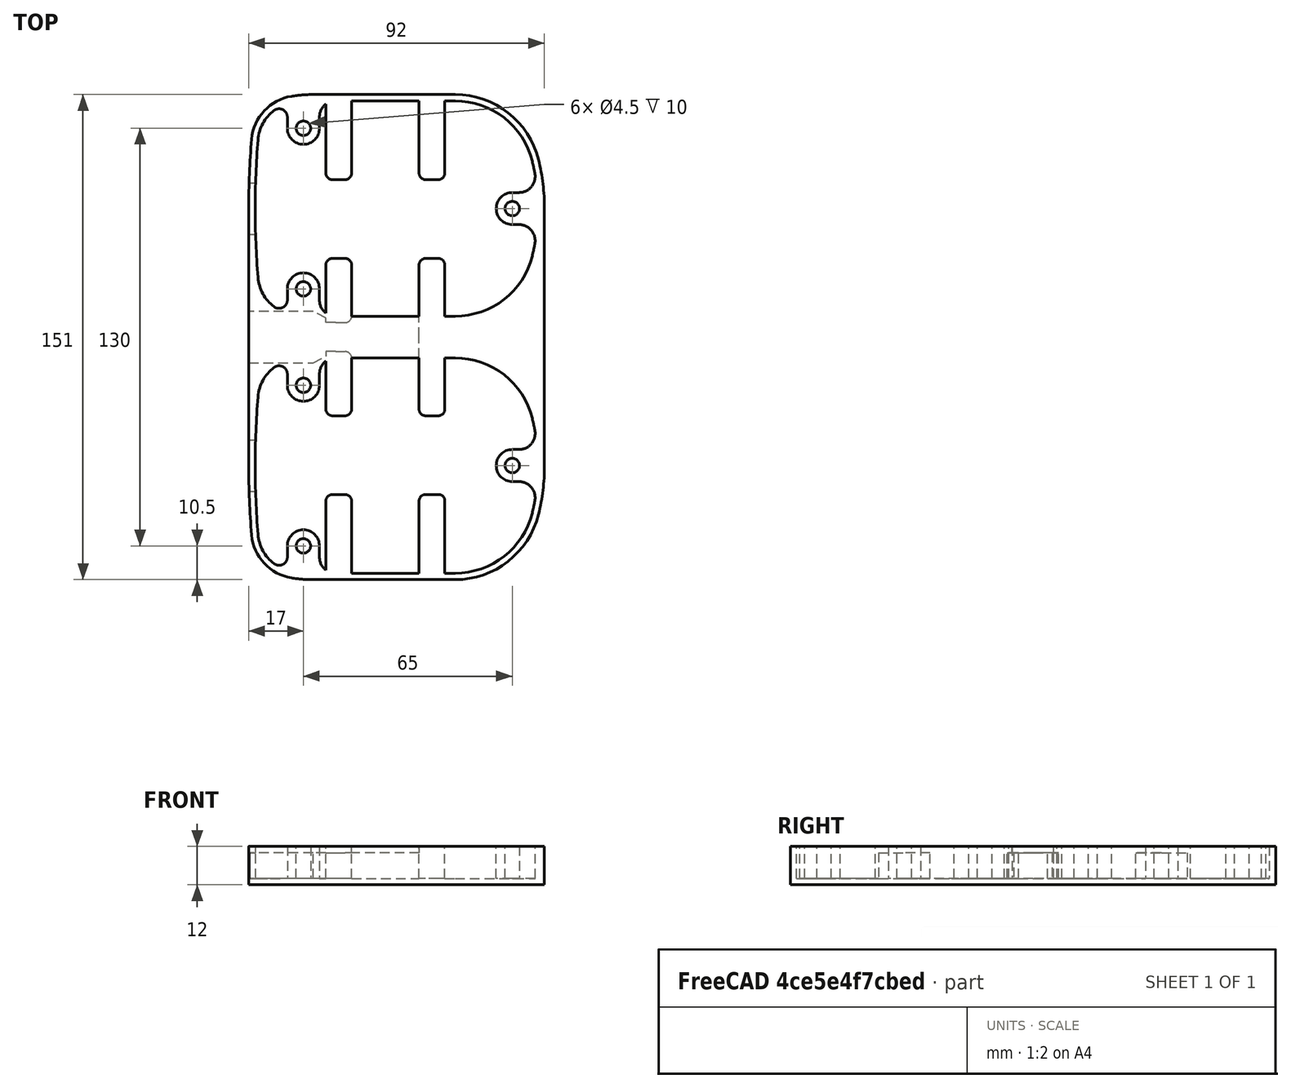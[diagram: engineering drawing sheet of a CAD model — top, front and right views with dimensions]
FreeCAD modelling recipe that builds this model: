
FCSTD DOCUMENT  (FreeCAD 1.0R39285 (Git))
Label: Makita LXT  - 18V - 2 x Bottom
License: Creative Commons Attribution 4.0
LicenseURL: https://creativecommons.org/licenses/by/4.0/
objects: Sketcher::SketchObject×6, PartDesign::Pocket×4, Mesh::Feature×3, PartDesign::Pad×2, Part::Feature×1, PartDesign::Body×1
note: 32 computed .brp shape members not serialized (recipe doc carries the construction recipe); baked Part::Feature solids carry a one-line shape summary decoded from their .brp

FEATURE [Mesh::Feature] XT60_top
  Placement = pos=(-27.47,40,-11) rot=(0,0,1;0rad)
FEATURE [Mesh::Feature] XT60_top001
  Placement = pos=(-27.47,-40,2) rot=(0,0,1;0rad)
FEATURE [Sketcher::SketchObject] Sketch
  ArcFitTolerance = 0
  AttachmentSupport = -> [XY_Plane]
  FullyConstrained = true
  MakeInternals = false
  MapMode = 5
  sketch-geometry (16):
    g0: ArcOfCircle CenterX=259.65 CenterY=40 CenterZ=0 NormalX=0 NormalY=0 NormalZ=1 AngleXU=0 Radius=259.65 StartAngle=3.05831 EndAngle=3.14159
    g1: ArcOfCircle CenterX=15.6319 CenterY=60.3702 CenterZ=0 NormalX=0 NormalY=0 NormalZ=1 AngleXU=0 Radius=14.7831 StartAngle=1.7292 EndAngle=3.05831
    g2: LineSegment StartX=20 StartY=75.5 StartZ=0 EndX=64.2 EndY=75.5 EndZ=0
    g3: ArcOfCircle CenterX=64.2 CenterY=48.7705 CenterZ=0 NormalX=0 NormalY=0 NormalZ=1 AngleXU=0 Radius=26.7295 StartAngle=0.24292 EndAngle=1.5708
    g4: ArcOfCircle CenterX=28.8084 CenterY=40 CenterZ=0 NormalX=0 NormalY=0 NormalZ=1 AngleXU=0 Radius=63.1916 StartAngle=0 EndAngle=0.24292
    g5: ArcOfCircle CenterX=20 CenterY=33.0247 CenterZ=0 NormalX=0 NormalY=0 NormalZ=1 AngleXU=0 Radius=42.4753 StartAngle=1.5708 EndAngle=1.7292
    g6: LineSegment StartX=0 StartY=40 StartZ=0 EndX=0 EndY=0 EndZ=0
    g7: LineSegment StartX=92 StartY=40 StartZ=0 EndX=92 EndY=0 EndZ=0
    g8: ArcOfCircle CenterX=259.65 CenterY=-40 CenterZ=0 NormalX=0 NormalY=0 NormalZ=1 AngleXU=0 Radius=259.65 StartAngle=3.14159 EndAngle=3.22488
    g9: ArcOfCircle CenterX=15.6319 CenterY=-60.3702 CenterZ=0 NormalX=0 NormalY=0 NormalZ=1 AngleXU=0 Radius=14.7831 StartAngle=3.22488 EndAngle=4.55399
    g10: LineSegment StartX=20 StartY=-75.5 StartZ=0 EndX=64.2 EndY=-75.5 EndZ=0
    g11: ArcOfCircle CenterX=64.2 CenterY=-48.7705 CenterZ=0 NormalX=0 NormalY=0 NormalZ=1 AngleXU=0 Radius=26.7295 StartAngle=4.71239 EndAngle=6.04026
    g12: ArcOfCircle CenterX=28.8084 CenterY=-40 CenterZ=0 NormalX=0 NormalY=0 NormalZ=1 AngleXU=0 Radius=63.1916 StartAngle=6.04026 EndAngle=6.28319
    g13: ArcOfCircle CenterX=20 CenterY=-33.0247 CenterZ=0 NormalX=0 NormalY=0 NormalZ=1 AngleXU=0 Radius=42.4753 StartAngle=4.55399 EndAngle=4.71239
    g14: LineSegment StartX=0 StartY=-40 StartZ=0 EndX=0 EndY=0 EndZ=0
    g15: LineSegment StartX=92 StartY=-40 StartZ=0 EndX=92 EndY=0 EndZ=0
  constraints (46):
    c: Horizontal(g2)
    c: DistanceX(g2) = 20
    c: DistanceY(g2) = 75.5
    c: DistanceX(g2,g2) = 44.2
    c: Tangent(g4,g3) = -1.5708
    c: Tangent(g3,g2) = 1.5708
    c: DistanceY(g3) = 55.2
    c: Tangent(g1,g0) = -1.5708
    c: Tangent(g5,g2) = 1.5708
    c: Tangent(g5,g1) = -1.5708
    c: DistanceX(g0) = 0.9
    c: DistanceX(g1) = 13.3
    c: DistanceY(g0) = 61.6
    c: Coincident(g6,g-1)
    c: Vertical(g6)
    c: PointOnObject(g7,g-1)
    c: Vertical(g7)
    c: Equal(g7,g6)
    c: DistanceY(g0) = 40
    c: DistanceX(g4) = 92
    c: Tangent(g7,g4) = 1.5708
    c: Tangent(g6,g0) = -1.5708
    c: Horizontal(g10)
    c: Tangent(g12,g11) = -1.5708
    c: Tangent(g11,g10) = -1.5708
    c: Tangent(g9,g8) = -1.5708
    c: Tangent(g13,g10) = -1.5708
    c: Tangent(g13,g9) = -1.5708
    c: Vertical(g14)
    c: Vertical(g15)
    c: Equal(g15,g14)
    c: Tangent(g15,g12) = -1.5708
    c: Tangent(g14,g8) = 1.5708
    c: Radius(g8) = 259.65  'Radius1'
    c: Radius(g9) = 14.7831  'Radius2'
    c: Radius(g13) = 42.4753  'Radius3'
    c: Radius(g11) = 26.7295  'Radius4'
    c: Radius(g12) = 63.1916  'Radius5'
    c: Coincident(g14,g6)
    c: Coincident(g15,g7)
    c: Equal(g12,g4)
    c: Equal(g11,g3)
    c: Equal(g5,g13)
    c: Equal(g9,g1)
    c: Symmetric(g8,g0,g-1)
    c: Symmetric(g1,g9,g-1)
FEATURE [PartDesign::Pad] Pad
  Direction = (0,0,1)
  Length = 12
  Length2 = 10
  Profile = -> Sketch
  ReferenceAxis = -> Sketch [N_Axis]
  Suppressed = false
  Type = 0
FEATURE [Sketcher::SketchObject] Sketch001
  ArcFitTolerance = 0
  AttachmentSupport = -> [Pad]
  ExternalGeometry = -> [Sketch]
  FullyConstrained = false
  MakeInternals = false
  MapMode = 5
  Placement = pos=(0,0,12) rot=(0,0,1;0rad)
  expr: Constraints[4] = <<Sketch>>.Constraints.Radius1 - 2 mm
  expr: Constraints[5] = <<Sketch>>.Constraints.Radius4 - 2 mm
  expr: Constraints[6] = <<Sketch>>.Constraints.Radius5 - 2 mm
  sketch-geometry (68):
    g0: ArcOfCircle CenterX=15.6319 CenterY=-60.3702 CenterZ=0 NormalX=0 NormalY=0 NormalZ=1 AngleXU=0 Radius=12.7831 StartAngle=3.22488 EndAngle=4.0613
    g1: ArcOfCircle CenterX=64.2 CenterY=-48.7705 CenterZ=0 NormalX=0 NormalY=0 NormalZ=1 AngleXU=0 Radius=24.7295 StartAngle=4.71239 EndAngle=6.04026
    g2: ArcOfCircle CenterX=28.8084 CenterY=-40 CenterZ=0 NormalX=0 NormalY=0 NormalZ=1 AngleXU=0 Radius=61.1916 StartAngle=6.04026 EndAngle=6.10427
    g3: ArcOfCircle CenterX=259.65 CenterY=-40 CenterZ=0 NormalX=0 NormalY=0 NormalZ=1 AngleXU=0 Radius=257.65 StartAngle=3.14159 EndAngle=3.22488
    g4: LineSegment StartX=27 StartY=-73.5 StartZ=0 EndX=64.2 EndY=-73.5 EndZ=0
    g5: LineSegment [constr] StartX=88.2034 StartY=-54.7189 StartZ=0 EndX=90.1447 EndY=-55.2 EndZ=0
    g6: LineSegment [constr] StartX=2 StartY=-40 StartZ=0 EndX=90 EndY=-40 EndZ=0
    g7: ArcOfCircle CenterX=15.6319 CenterY=-19.6298 CenterZ=0 NormalX=0 NormalY=0 NormalZ=1 AngleXU=0 Radius=12.7831 StartAngle=2.22189 EndAngle=3.05831
    g8: ArcOfCircle CenterX=259.65 CenterY=-40 CenterZ=0 NormalX=0 NormalY=0 NormalZ=1 AngleXU=0 Radius=257.65 StartAngle=3.05831 EndAngle=3.14159
    g9: ArcOfCircle CenterX=64.2 CenterY=-31.2295 CenterZ=0 NormalX=0 NormalY=0 NormalZ=1 AngleXU=0 Radius=24.7295 StartAngle=0.24292 EndAngle=1.5708
    g10: ArcOfCircle CenterX=28.8084 CenterY=-40 CenterZ=0 NormalX=0 NormalY=0 NormalZ=1 AngleXU=0 Radius=61.1916 StartAngle=0.178916 EndAngle=0.24292
    g11: LineSegment StartX=27 StartY=-6.5 StartZ=0 EndX=64.2 EndY=-6.5 EndZ=0
    g12: Circle CenterX=17 CenterY=-15 CenterZ=0 NormalX=0 NormalY=0 NormalZ=1 AngleXU=0 Radius=2.25
    g13: Circle CenterX=17 CenterY=-65 CenterZ=0 NormalX=0 NormalY=0 NormalZ=1 AngleXU=0 Radius=2.25
    g14: Circle CenterX=82 CenterY=-40 CenterZ=0 NormalX=0 NormalY=0 NormalZ=1 AngleXU=0 Radius=2.25
    g15: ArcOfCircle CenterX=17 CenterY=-15 CenterZ=0 NormalX=0 NormalY=0 NormalZ=1 AngleXU=0 Radius=5 StartAngle=3.14159 EndAngle=6.28319
    g16: ArcOfCircle CenterX=17 CenterY=-65 CenterZ=0 NormalX=0 NormalY=0 NormalZ=1 AngleXU=0 Radius=5 StartAngle=0 EndAngle=3.14159
    g17: ArcOfCircle CenterX=82 CenterY=-40 CenterZ=0 NormalX=0 NormalY=0 NormalZ=1 AngleXU=0 Radius=5 StartAngle=1.5708 EndAngle=4.71239
    g18: LineSegment StartX=22 StartY=-15 StartZ=0 EndX=22 EndY=-11.5 EndZ=0
    g19: LineSegment StartX=12 StartY=-15 StartZ=0 EndX=12 EndY=-11.5 EndZ=0
    g20: LineSegment StartX=12 StartY=-65 StartZ=0 EndX=12 EndY=-68.5 EndZ=0
    g21: LineSegment StartX=22 StartY=-65 StartZ=0 EndX=22 EndY=-68.5 EndZ=0
    g22: LineSegment StartX=82 StartY=-45 StartZ=0 EndX=84.103 EndY=-45 EndZ=0
    g23: LineSegment StartX=82 StartY=-35 StartZ=0 EndX=84.103 EndY=-35 EndZ=0
    g24: ArcOfCircle CenterX=84.103 CenterY=-30 CenterZ=0 NormalX=0 NormalY=0 NormalZ=1 AngleXU=0 Radius=5 StartAngle=4.71239 EndAngle=6.4621
    g25: ArcOfCircle CenterX=84.103 CenterY=-50 CenterZ=0 NormalX=0 NormalY=0 NormalZ=1 AngleXU=0 Radius=5 StartAngle=6.10427 EndAngle=7.85398
    g26: ArcOfCircle CenterX=27 CenterY=-11.5 CenterZ=0 NormalX=0 NormalY=0 NormalZ=1 AngleXU=0 Radius=5 StartAngle=1.5708 EndAngle=3.14159
    g27: ArcOfCircle CenterX=9.43759 CenterY=-11.5 CenterZ=0 NormalX=0 NormalY=0 NormalZ=1 AngleXU=0 Radius=2.56241 StartAngle=0 EndAngle=2.22189
    g28: ArcOfCircle CenterX=9.43759 CenterY=-68.5 CenterZ=0 NormalX=0 NormalY=0 NormalZ=1 AngleXU=0 Radius=2.56241 StartAngle=4.0613 EndAngle=6.28319
    g29: ArcOfCircle CenterX=27 CenterY=-68.5 CenterZ=0 NormalX=0 NormalY=0 NormalZ=1 AngleXU=0 Radius=5 StartAngle=3.14159 EndAngle=4.71239
    g30: ArcOfCircle [constr] CenterX=28.8084 CenterY=-40 CenterZ=0 NormalX=0 NormalY=0 NormalZ=1 AngleXU=0 Radius=61.1916 StartAngle=6.10427 EndAngle=6.4621
    g31: LineSegment [constr] StartX=27 StartY=-6.5 StartZ=0 EndX=20 EndY=-6.5 EndZ=0
    g32: ArcOfCircle [constr] CenterX=20 CenterY=-46.9753 CenterZ=0 NormalX=0 NormalY=0 NormalZ=1 AngleXU=0 Radius=40.4753 StartAngle=1.5708 EndAngle=1.7292
    g33: ArcOfCircle [constr] CenterX=15.6319 CenterY=-19.6298 CenterZ=0 NormalX=0 NormalY=0 NormalZ=1 AngleXU=0 Radius=12.7831 StartAngle=1.7292 EndAngle=2.22189
    g34: ArcOfCircle CenterX=15.6319 CenterY=60.3702 CenterZ=0 NormalX=0 NormalY=0 NormalZ=1 AngleXU=0 Radius=12.7831 StartAngle=2.22189 EndAngle=3.05831
    g35: ArcOfCircle CenterX=64.2 CenterY=48.7705 CenterZ=0 NormalX=0 NormalY=0 NormalZ=1 AngleXU=0 Radius=24.7295 StartAngle=0.24292 EndAngle=1.5708
    g36: ArcOfCircle CenterX=28.8084 CenterY=40 CenterZ=0 NormalX=0 NormalY=0 NormalZ=1 AngleXU=0 Radius=61.1916 StartAngle=0.178916 EndAngle=0.24292
    g37: ArcOfCircle CenterX=259.65 CenterY=40 CenterZ=0 NormalX=0 NormalY=0 NormalZ=1 AngleXU=0 Radius=257.65 StartAngle=3.05831 EndAngle=3.14159
    g38: LineSegment StartX=27 StartY=73.5 StartZ=0 EndX=64.2 EndY=73.5 EndZ=0
    g39: LineSegment [constr] StartX=88.2034 StartY=54.7189 StartZ=0 EndX=90.1447 EndY=55.2 EndZ=0
    g40: LineSegment [constr] StartX=2 StartY=40 StartZ=0 EndX=90 EndY=40 EndZ=0
    g41: ArcOfCircle CenterX=15.6319 CenterY=19.6298 CenterZ=0 NormalX=0 NormalY=0 NormalZ=1 AngleXU=0 Radius=12.7831 StartAngle=3.22488 EndAngle=4.0613
    g42: ArcOfCircle CenterX=259.65 CenterY=40 CenterZ=0 NormalX=0 NormalY=0 NormalZ=1 AngleXU=0 Radius=257.65 StartAngle=3.14159 EndAngle=3.22488
    g43: ArcOfCircle CenterX=64.2 CenterY=31.2295 CenterZ=0 NormalX=0 NormalY=0 NormalZ=1 AngleXU=0 Radius=24.7295 StartAngle=4.71239 EndAngle=6.04026
    g44: ArcOfCircle CenterX=28.8084 CenterY=40 CenterZ=0 NormalX=0 NormalY=0 NormalZ=1 AngleXU=0 Radius=61.1916 StartAngle=6.04026 EndAngle=6.10427
    g45: LineSegment StartX=27 StartY=6.5 StartZ=0 EndX=64.2 EndY=6.5 EndZ=0
    g46: Circle CenterX=17 CenterY=15 CenterZ=0 NormalX=0 NormalY=0 NormalZ=1 AngleXU=0 Radius=2.25
    g47: Circle CenterX=17 CenterY=65 CenterZ=0 NormalX=0 NormalY=0 NormalZ=1 AngleXU=0 Radius=2.25
    g48: Circle CenterX=82 CenterY=40 CenterZ=0 NormalX=0 NormalY=0 NormalZ=1 AngleXU=0 Radius=2.25
    g49: ArcOfCircle CenterX=17 CenterY=15 CenterZ=0 NormalX=0 NormalY=0 NormalZ=1 AngleXU=0 Radius=5 StartAngle=4e-16 EndAngle=3.14159
    g50: ArcOfCircle CenterX=17 CenterY=65 CenterZ=0 NormalX=0 NormalY=0 NormalZ=1 AngleXU=0 Radius=5 StartAngle=3.14159 EndAngle=6.28319
    g51: ArcOfCircle CenterX=82 CenterY=40 CenterZ=0 NormalX=0 NormalY=0 NormalZ=1 AngleXU=0 Radius=5 StartAngle=1.5708 EndAngle=4.71239
    g52: LineSegment StartX=22 StartY=15 StartZ=0 EndX=22 EndY=11.5 EndZ=0
    g53: LineSegment StartX=12 StartY=15 StartZ=0 EndX=12 EndY=11.5 EndZ=0
    g54: LineSegment StartX=12 StartY=65 StartZ=0 EndX=12 EndY=68.5 EndZ=0
    g55: LineSegment StartX=22 StartY=65 StartZ=0 EndX=22 EndY=68.5 EndZ=0
    g56: LineSegment StartX=82 StartY=45 StartZ=0 EndX=84.103 EndY=45 EndZ=0
    g57: LineSegment StartX=82 StartY=35 StartZ=0 EndX=84.103 EndY=35 EndZ=0
    g58: ArcOfCircle CenterX=84.103 CenterY=30 CenterZ=0 NormalX=0 NormalY=0 NormalZ=1 AngleXU=0 Radius=5 StartAngle=6.10427 EndAngle=7.85398
    g59: ArcOfCircle CenterX=84.103 CenterY=50 CenterZ=0 NormalX=0 NormalY=0 NormalZ=1 AngleXU=0 Radius=5 StartAngle=4.71239 EndAngle=6.4621
    g60: ArcOfCircle CenterX=27 CenterY=11.5 CenterZ=0 NormalX=0 NormalY=0 NormalZ=1 AngleXU=0 Radius=5 StartAngle=3.14159 EndAngle=4.71239
    g61: ArcOfCircle CenterX=9.43759 CenterY=11.5 CenterZ=0 NormalX=0 NormalY=0 NormalZ=1 AngleXU=0 Radius=2.56241 StartAngle=4.0613 EndAngle=6.28319
    g62: ArcOfCircle CenterX=9.43759 CenterY=68.5 CenterZ=0 NormalX=0 NormalY=0 NormalZ=1 AngleXU=0 Radius=2.56241 StartAngle=0 EndAngle=2.22189
    g63: ArcOfCircle CenterX=27 CenterY=68.5 CenterZ=0 NormalX=0 NormalY=0 NormalZ=1 AngleXU=0 Radius=5 StartAngle=1.5708 EndAngle=3.14159
    g64: ArcOfCircle [constr] CenterX=28.8084 CenterY=40 CenterZ=0 NormalX=0 NormalY=0 NormalZ=1 AngleXU=0 Radius=61.1916 StartAngle=6.10427 EndAngle=6.4621
    g65: LineSegment [constr] StartX=27 StartY=6.5 StartZ=0 EndX=20 EndY=6.5 EndZ=0
    g66: ArcOfCircle [constr] CenterX=20 CenterY=46.9753 CenterZ=0 NormalX=0 NormalY=0 NormalZ=1 AngleXU=0 Radius=40.4753 StartAngle=4.55399 EndAngle=4.71239
    g67: ArcOfCircle [constr] CenterX=15.6319 CenterY=19.6298 CenterZ=0 NormalX=0 NormalY=0 NormalZ=1 AngleXU=0 Radius=12.7831 StartAngle=4.0613 EndAngle=4.55399
  constraints (164):
    c: Coincident(g0,g-4)
    c: Coincident(g2,g-8)
    c: Coincident(g2,g1)
    c: Coincident(g3,g-3)
    c: Radius(g3) = 257.65
    c: Radius(g1) = 24.7295
    c: Radius(g2) = 61.1916
    c: Coincident(g4,g1)
    c: Horizontal(g4)
    c: Vertical(g-7,g1)
    c: Horizontal(g-3,g3)
    c: Coincident(g5,g1)
    c: Coincident(g5,g-8)
    c: Perpendicular(g-8,g5)
    c: Coincident(g6,g3)
    c: Coincident(g10,g9)
    c: Coincident(g8,g7)
    c: Coincident(g11,g9)
    c: Tangent(g3,g0) = -1.5708
    c: Equal(g8,g3)
    c: Equal(g0,g7)
    c: Equal(g1,g9)
    c: Equal(g2,g10)
    c: Symmetric(g1,g9,g6)
    c: Horizontal(g11)
    c: Symmetric(g1,g9,g6)
    c: Symmetric(g7,g0,g6)
    c: Coincident(g8,g3)
    c: PointOnObject(g14,g6)
    c: Equal(g12,g13)
    c: Equal(g13,g14)
    c: Symmetric(g12,g13,g6)
    c: DistanceX(g-3,g12) = 17
    c: DistanceY(g-3,g12) = 25
    c: Diameter(g12) = 4.5
    c: DistanceX(g12,g14) = 65
    c: Coincident(g15,g12)
    c: Coincident(g16,g13)
    c: Coincident(g17,g14)
    c: Vertical(g17,g14)
    c: Vertical(g14,g17)
    c: Horizontal(g15,g12)
    c: Horizontal(g12,g15)
    c: Horizontal(g16,g13)
    c: Horizontal(g13,g16)
    c: Equal(g16,g15)
    c: Equal(g15,g17)
    c: Diameter(g15) = 10
    c: Coincident(g18,g15)
    c: Vertical(g18)
    c: Coincident(g19,g15)
    c: Coincident(g20,g16)
    c: Vertical(g20)
    c: Coincident(g21,g16)
    c: Vertical(g21)
    c: Coincident(g22,g17)
    c: Coincident(g23,g17)
    c: Equal(g23,g22)
    c: Equal(g21,g18)
    c: Equal(g19,g20)
    c: Horizontal(g22)
    c: Coincident(g26,g18)
    c: Equal(g29,g26)
    c: Equal(g28,g27)
    c: Tangent(g27,g19) = -1.5708
    c: Equal(g18,g19)
    c: Tangent(g29,g21) = -1.5708
    c: Tangent(g28,g20) = 1.5708
    c: Equal(g26,g15)
    c: Tangent(g24,g23) = -1.5708
    c: Tangent(g25,g22) = 1.5708
    c: Equal(g24,g17)
    c: Tangent(g10,g24) = -1.5708
    c: Tangent(g2,g25) = -1.5708
    c: Coincident(g30,g2)
    c: Coincident(g30,g10)
    c: Coincident(g30,g2)
    c: Symmetric(g10,g2,g6)
    c: PointOnObject(g6,g30)
    c: Tangent(g11,g26) = 1.5708
    c: Tangent(g7,g27) = -1.5708
    c: Coincident(g31,g11)
    c: Equal(g33,g7)
    c: Tangent(g33,g32) = -1.5708
    c: Tangent(g4,g29) = -1.5708
    c: Tangent(g0,g28) = -1.5708
    c: DistanceY(g-7,g1) = 2
    c: Vertical(g19)
    c: Tangent(g33,g7) = -1.5708
    c: Tangent(g32,g31) = -1.5708
    c: Symmetric(g32,g-5,g6)
    c: Coincident(g36,g35)
    c: Radius(g37) = 257.65
    c: Radius(g35) = 24.7295
    c: Radius(g36) = 61.1916
    c: Coincident(g38,g35)
    c: Horizontal(g38)
    c: Coincident(g39,g35)
    c: Coincident(g40,g37)
    c: Coincident(g44,g43)
    c: Coincident(g42,g41)
    c: Coincident(g45,g43)
    c: Tangent(g37,g34) = -1.5708
    c: Equal(g42,g37)
    c: Equal(g34,g41)
    c: Equal(g35,g43)
    c: Equal(g36,g44)
    c: Symmetric(g35,g43,g40)
    c: Horizontal(g45)
    c: Symmetric(g35,g43,g40)
    c: Symmetric(g41,g34,g40)
    c: Coincident(g42,g37)
    c: PointOnObject(g48,g40)
    c: Equal(g46,g47)
    c: Equal(g47,g48)
    c: Symmetric(g46,g47,g40)
    c: Diameter(g46) = 4.5
    c: Coincident(g49,g46)
    c: Coincident(g50,g47)
    c: Coincident(g51,g48)
    c: Equal(g50,g49)
    c: Equal(g49,g51)
    c: Diameter(g49) = 10
    c: Coincident(g52,g49)
    c: Vertical(g52)
    c: Coincident(g53,g49)
    c: Coincident(g54,g50)
    c: Vertical(g54)
    c: Coincident(g55,g50)
    c: Vertical(g55)
    c: Coincident(g56,g51)
    c: Coincident(g57,g51)
    c: Equal(g57,g56)
    c: Equal(g55,g52)
    c: Equal(g53,g54)
    c: Horizontal(g56)
    c: Coincident(g60,g52)
    c: Equal(g63,g60)
    c: Equal(g62,g61)
    c: Tangent(g61,g53) = 1.5708
    c: Equal(g52,g53)
    c: Tangent(g63,g55) = 1.5708
    c: Tangent(g62,g54) = -1.5708
    c: Equal(g60,g49)
    c: Tangent(g58,g57) = 1.5708
    c: Tangent(g59,g56) = -1.5708
    c: Equal(g58,g51)
    c: Tangent(g44,g58) = -1.5708
    c: Tangent(g36,g59) = -1.5708
    c: Coincident(g64,g36)
    c: Coincident(g64,g44)
    c: Coincident(g64,g36)
    c: Symmetric(g44,g36,g40)
    c: PointOnObject(g40,g64)
    c: Tangent(g45,g60) = -1.5708
    c: Tangent(g41,g61) = -1.5708
    c: Coincident(g65,g45)
    c: Equal(g67,g41)
    c: Tangent(g67,g66) = -1.5708
    c: Tangent(g38,g63) = 1.5708
    c: Tangent(g34,g62) = -1.5708
    c: Vertical(g53)
    c: Tangent(g67,g41) = -1.5708
    c: Tangent(g66,g65) = 1.5708
FEATURE [PartDesign::Pocket] Pocket
  BaseFeature = -> Pad
  Direction = (0,0,-1)
  Length = 10
  Length2 = 5
  Profile = -> Sketch001
  ReferenceAxis = -> Sketch001 [N_Axis]
  Suppressed = false
  Type = 0
FEATURE [Mesh::Feature] makita_t_mount_M3
  Placement = pos=(-27.47,-40,0) rot=(0,0,1;0rad)
FEATURE [Sketcher::SketchObject] Sketch002
  ArcFitTolerance = 0
  AttachmentSupport = -> [YZ_Plane]
  FullyConstrained = false
  MakeInternals = false
  MapMode = 5
  Placement = pos=(0,0,0) rot=(0.57735,0.57735,0.57735;2.0944rad)
  sketch-geometry (10):
    g0: LineSegment StartX=-48 StartY=10 StartZ=0 EndX=-48 EndY=2 EndZ=0
    g1: LineSegment StartX=-48 StartY=2 StartZ=0 EndX=-32 EndY=2 EndZ=0
    g2: LineSegment StartX=-32 StartY=2 StartZ=0 EndX=-32 EndY=10 EndZ=0
    g3: LineSegment StartX=-32 StartY=10 StartZ=0 EndX=-48 EndY=10 EndZ=0
    g4: GeomPoint [constr] X=-40 Y=6 Z=0
    g5: LineSegment StartX=48 StartY=10 StartZ=0 EndX=48 EndY=2 EndZ=0
    g6: LineSegment StartX=48 StartY=2 StartZ=0 EndX=32 EndY=2 EndZ=0
    g7: LineSegment StartX=32 StartY=2 StartZ=0 EndX=32 EndY=10 EndZ=0
    g8: LineSegment StartX=32 StartY=10 StartZ=0 EndX=48 EndY=10 EndZ=0
    g9: GeomPoint [constr] X=40 Y=6 Z=0
  constraints (22):
    c: Coincident(g0,g1)
    c: Coincident(g1,g2)
    c: Coincident(g2,g3)
    c: Coincident(g3,g0)
    c: Horizontal(g1)
    c: Horizontal(g3)
    c: Vertical(g0)
    c: Vertical(g2)
    c: Symmetric(g1,g0,g4)
    c: DistanceX(g3,g3) = 16
    c: DistanceY(g0,g0) = 8
    c: DistanceY(g-1,g4) = 6
    c: DistanceX(g4,g-1) = 40
    c: Coincident(g5,g6)
    c: Coincident(g6,g7)
    c: Coincident(g7,g8)
    c: Coincident(g8,g5)
    c: Horizontal(g6)
    c: Horizontal(g8)
    c: Vertical(g5)
    c: Vertical(g7)
    c: Symmetric(g6,g5,g9)
FEATURE [PartDesign::Pocket] Pocket001
  BaseFeature = -> Pocket
  Direction = (-1,0,0)
  Length = 10
  Length2 = 5
  Profile = -> Sketch002
  ReferenceAxis = -> Sketch002 [N_Axis]
  Reversed = true
  Suppressed = false
  Type = 0
FEATURE [Sketcher::SketchObject] Sketch003
  ArcFitTolerance = 0
  AttachmentSupport = -> [XZ_Plane]
  FullyConstrained = true
  MakeInternals = false
  MapMode = 5
  Placement = pos=(0,0,0) rot=(1,0,0;1.5708rad)
  sketch-geometry (5):
    g0: LineSegment StartX=27 StartY=10 StartZ=0 EndX=27 EndY=2 EndZ=0
    g1: LineSegment StartX=27 StartY=2 StartZ=0 EndX=57 EndY=2 EndZ=0
    g2: LineSegment StartX=57 StartY=2 StartZ=0 EndX=57 EndY=10 EndZ=0
    g3: LineSegment StartX=57 StartY=10 StartZ=0 EndX=27 EndY=10 EndZ=0
    g4: GeomPoint [constr] X=42 Y=6 Z=0
  constraints (13):
    c: Coincident(g0,g1)
    c: Coincident(g1,g2)
    c: Coincident(g2,g3)
    c: Coincident(g3,g0)
    c: Horizontal(g1)
    c: Horizontal(g3)
    c: Vertical(g0)
    c: Vertical(g2)
    c: Symmetric(g1,g0,g4)
    c: DistanceY(g2,g2) = 8
    c: DistanceX(g3,g3) = 30
    c: DistanceX(g4) = 42
    c: DistanceY(g4) = 6
FEATURE [PartDesign::Pocket] Pocket002
  BaseFeature = -> Pocket001
  Direction = (0,1,-2e-16)
  Length = 13
  Length2 = 5
  Midplane = true
  Profile = -> Sketch003
  ReferenceAxis = -> Sketch003 [N_Axis]
  Suppressed = false
  Type = 0
FEATURE [Part::Feature] makita_t_mount_M004
  Placement = pos=(0,0,15) rot=(0,0,1;0rad)
  shape: bbox 92.05 x 71 x 21.06 mm, 5616 faces, 0 solids (baked)
FEATURE [PartDesign::Body] Body  label="Makita 18V x 2 base"
  AllowCompound = false
  Group = -> [Sketch,Pad,Sketch001,Pocket,Sketch002,Pocket001,Sketch003,Pocket002,Sketch007,Pocket003,Sketch008,Pad001]
  Origin = -> Origin
  Tip = -> Pad001
FEATURE [Sketcher::SketchObject] Sketch007
  ArcFitTolerance = 0
  AttachmentSupport = -> [Pocket003]
  FullyConstrained = false
  MakeInternals = false
  MapMode = 5
  Placement = pos=(0,0,2) rot=(0,0,1;0rad)
  sketch-geometry (6):
    g0: LineSegment StartX=0 StartY=8 StartZ=0 EndX=0 EndY=-8 EndZ=0
    g1: LineSegment StartX=0 StartY=-8 StartZ=0 EndX=20 EndY=-8 EndZ=0
    g2: LineSegment StartX=20 StartY=8 StartZ=0 EndX=0 EndY=8 EndZ=0
    g3: LineSegment StartX=27 StartY=4.5 StartZ=0 EndX=27 EndY=-4.5 EndZ=0
    g4: LineSegment StartX=27 StartY=4.5 StartZ=0 EndX=20 EndY=8 EndZ=0
    g5: LineSegment StartX=20 StartY=-8 StartZ=0 EndX=27 EndY=-4.5 EndZ=0
  constraints (16):
    c: PointOnObject(g0,g-2)
    c: Coincident(g0,g1)
    c: Horizontal(g1)
    c: Coincident(g2,g0)
    c: Horizontal(g2)
    c: Symmetric(g0,g0,g-1)
    c: Equal(g2,g1)
    c: DistanceY(g0,g0) = 16
    c: DistanceX(g2,g2) = 20
    c: DistanceY(g3,g3) = 9
    c: Vertical(g3)
    c: Coincident(g4,g3)
    c: Coincident(g5,g1)
    c: Coincident(g5,g3)
    c: Equal(g4,g5)
    c: Coincident(g4,g2)
FEATURE [PartDesign::Pocket] Pocket003
  BaseFeature = -> Pocket002
  Direction = (0,0,-1)
  Length = 8
  Length2 = 5
  Profile = -> Sketch007
  ReferenceAxis = -> Sketch007 [N_Axis]
  Reversed = true
  Suppressed = false
  Type = 0
FEATURE [Sketcher::SketchObject] Sketch008
  ArcFitTolerance = 0
  AttachmentSupport = -> [Pocket003]
  ExternalGeometry = -> [Pocket003]
  FullyConstrained = false
  MakeInternals = false
  MapMode = 5
  Placement = pos=(0,0,2) rot=(0,0,1;0rad)
  sketch-geometry (48):
    g0: LineSegment StartX=24 StartY=-4.5 StartZ=0 EndX=24 EndY=-22.5 EndZ=0
    g1: LineSegment StartX=26 StartY=-24.5 StartZ=0 EndX=30 EndY=-24.5 EndZ=0
    g2: LineSegment StartX=32 StartY=-22.5 StartZ=0 EndX=32 EndY=-6.5 EndZ=0
    g3: LineSegment StartX=30 StartY=-4.5 StartZ=0 EndX=24 EndY=-4.5 EndZ=0
    g4: LineSegment StartX=53 StartY=0 StartZ=0 EndX=53 EndY=-22.5 EndZ=0
    g5: LineSegment StartX=55 StartY=-24.5 StartZ=0 EndX=59 EndY=-24.5 EndZ=0
    g6: LineSegment StartX=61 StartY=-22.5 StartZ=0 EndX=61 EndY=0 EndZ=0
    g7: LineSegment StartX=24 StartY=-51 StartZ=0 EndX=24 EndY=-73.5 EndZ=0
    g8: LineSegment StartX=24 StartY=-73.5 StartZ=0 EndX=32 EndY=-73.5 EndZ=0
    g9: LineSegment StartX=32 StartY=-73.5 StartZ=0 EndX=32 EndY=-51 EndZ=0
    g10: LineSegment StartX=30 StartY=-49 StartZ=0 EndX=26 EndY=-49 EndZ=0
    g11: LineSegment StartX=53 StartY=-51 StartZ=0 EndX=53 EndY=-73.5 EndZ=0
    g12: LineSegment StartX=53 StartY=-73.5 StartZ=0 EndX=61 EndY=-73.5 EndZ=0
    g13: LineSegment StartX=61 StartY=-73.5 StartZ=0 EndX=61 EndY=-51 EndZ=0
    g14: LineSegment StartX=59 StartY=-49 StartZ=0 EndX=55 EndY=-49 EndZ=0
    g15: ArcOfCircle CenterX=59 CenterY=-22.5 CenterZ=0 NormalX=0 NormalY=0 NormalZ=1 AngleXU=0 Radius=2 StartAngle=4.71239 EndAngle=6.28319
    g16: ArcOfCircle CenterX=55 CenterY=-22.5 CenterZ=0 NormalX=0 NormalY=0 NormalZ=1 AngleXU=0 Radius=2 StartAngle=3.14159 EndAngle=4.71239
    g17: ArcOfCircle CenterX=30 CenterY=-22.5 CenterZ=0 NormalX=0 NormalY=0 NormalZ=1 AngleXU=0 Radius=2 StartAngle=4.71239 EndAngle=6.28319
    g18: ArcOfCircle CenterX=26 CenterY=-22.5 CenterZ=0 NormalX=0 NormalY=0 NormalZ=1 AngleXU=0 Radius=2 StartAngle=3.14159 EndAngle=4.71239
    g19: ArcOfCircle CenterX=26 CenterY=-51 CenterZ=0 NormalX=0 NormalY=0 NormalZ=1 AngleXU=0 Radius=2 StartAngle=1.5708 EndAngle=3.14159
    g20: ArcOfCircle CenterX=30 CenterY=-51 CenterZ=0 NormalX=0 NormalY=0 NormalZ=1 AngleXU=0 Radius=2 StartAngle=0 EndAngle=1.5708
    g21: ArcOfCircle CenterX=55 CenterY=-51 CenterZ=0 NormalX=0 NormalY=0 NormalZ=1 AngleXU=0 Radius=2 StartAngle=1.5708 EndAngle=3.14159
    g22: ArcOfCircle CenterX=59 CenterY=-51 CenterZ=0 NormalX=0 NormalY=0 NormalZ=1 AngleXU=0 Radius=2 StartAngle=-9e-16 EndAngle=1.5708
    g23: ArcOfCircle CenterX=30 CenterY=-6.5 CenterZ=0 NormalX=0 NormalY=0 NormalZ=1 AngleXU=0 Radius=2 StartAngle=0 EndAngle=1.5708
    g24: LineSegment StartX=24 StartY=4.5 StartZ=0 EndX=24 EndY=22.5 EndZ=0
    g25: LineSegment StartX=26 StartY=24.5 StartZ=0 EndX=30 EndY=24.5 EndZ=0
    g26: LineSegment StartX=32 StartY=22.5 StartZ=0 EndX=32 EndY=6.5 EndZ=0
    g27: LineSegment StartX=30 StartY=4.5 StartZ=0 EndX=24 EndY=4.5 EndZ=0
    g28: LineSegment StartX=53 StartY=0 StartZ=0 EndX=53 EndY=22.5 EndZ=0
    g29: LineSegment StartX=55 StartY=24.5 StartZ=0 EndX=59 EndY=24.5 EndZ=0
    g30: LineSegment StartX=61 StartY=22.5 StartZ=0 EndX=61 EndY=0 EndZ=0
    g31: LineSegment StartX=24 StartY=51 StartZ=0 EndX=24 EndY=73.5 EndZ=0
    g32: LineSegment StartX=24 StartY=73.5 StartZ=0 EndX=32 EndY=73.5 EndZ=0
    g33: LineSegment StartX=32 StartY=73.5 StartZ=0 EndX=32 EndY=51 EndZ=0
    g34: LineSegment StartX=30 StartY=49 StartZ=0 EndX=26 EndY=49 EndZ=0
    g35: LineSegment StartX=53 StartY=51 StartZ=0 EndX=53 EndY=73.5 EndZ=0
    g36: LineSegment StartX=53 StartY=73.5 StartZ=0 EndX=61 EndY=73.5 EndZ=0
    g37: LineSegment StartX=61 StartY=73.5 StartZ=0 EndX=61 EndY=51 EndZ=0
    g38: LineSegment StartX=59 StartY=49 StartZ=0 EndX=55 EndY=49 EndZ=0
    g39: ArcOfCircle CenterX=59 CenterY=22.5 CenterZ=0 NormalX=0 NormalY=0 NormalZ=1 AngleXU=0 Radius=2 StartAngle=0 EndAngle=1.5708
    g40: ArcOfCircle CenterX=55 CenterY=22.5 CenterZ=0 NormalX=0 NormalY=0 NormalZ=1 AngleXU=0 Radius=2 StartAngle=1.5708 EndAngle=3.14159
    g41: ArcOfCircle CenterX=30 CenterY=22.5 CenterZ=0 NormalX=0 NormalY=0 NormalZ=1 AngleXU=0 Radius=2 StartAngle=0 EndAngle=1.5708
    g42: ArcOfCircle CenterX=26 CenterY=22.5 CenterZ=0 NormalX=0 NormalY=0 NormalZ=1 AngleXU=0 Radius=2 StartAngle=1.5708 EndAngle=3.14159
    g43: ArcOfCircle CenterX=26 CenterY=51 CenterZ=0 NormalX=0 NormalY=0 NormalZ=1 AngleXU=0 Radius=2 StartAngle=3.14159 EndAngle=4.71239
    g44: ArcOfCircle CenterX=30 CenterY=51 CenterZ=0 NormalX=0 NormalY=0 NormalZ=1 AngleXU=0 Radius=2 StartAngle=4.71239 EndAngle=6.28319
    g45: ArcOfCircle CenterX=55 CenterY=51 CenterZ=0 NormalX=0 NormalY=0 NormalZ=1 AngleXU=0 Radius=2 StartAngle=3.14159 EndAngle=4.71239
    g46: ArcOfCircle CenterX=59 CenterY=51 CenterZ=0 NormalX=0 NormalY=0 NormalZ=1 AngleXU=0 Radius=2 StartAngle=4.71239 EndAngle=6.28319
    g47: ArcOfCircle CenterX=30 CenterY=6.5 CenterZ=0 NormalX=0 NormalY=0 NormalZ=1 AngleXU=0 Radius=2 StartAngle=4.71239 EndAngle=6.28319
  constraints (116):
    c: Coincident(g3,g0)
    c: Horizontal(g1)
    c: Horizontal(g3)
    c: Vertical(g0)
    c: Vertical(g2)
    c: Horizontal(g5)
    c: Vertical(g4)
    c: Vertical(g6)
    c: Coincident(g7,g8)
    c: Coincident(g8,g9)
    c: Horizontal(g8)
    c: Horizontal(g10)
    c: Vertical(g7)
    c: Vertical(g9)
    c: Coincident(g11,g12)
    c: Coincident(g12,g13)
    c: Horizontal(g12)
    c: Horizontal(g14)
    c: Vertical(g11)
    c: Vertical(g13)
    c: Tangent(g5,g15) = -1.5708
    c: Tangent(g6,g15) = -1.5708
    c: Tangent(g4,g16) = -1.5708
    c: Tangent(g5,g16) = -1.5708
    c: Tangent(g2,g17) = -1.5708
    c: Tangent(g1,g17) = -1.5708
    c: Tangent(g0,g18) = -1.5708
    c: Tangent(g1,g18) = -1.5708
    c: Tangent(g7,g19) = -1.5708
    c: Tangent(g10,g19) = -1.5708
    c: Tangent(g9,g20) = -1.5708
    c: Tangent(g10,g20) = -1.5708
    c: Tangent(g11,g21) = -1.5708
    c: Tangent(g14,g21) = -1.5708
    c: Tangent(g13,g22) = -1.5708
    c: Tangent(g14,g22) = -1.5708
    c: Equal(g4,g11)
    c: Equal(g11,g9)
    c: Tangent(g2,g23) = -1.5708
    c: Tangent(g3,g23) = -1.5708
    c: Equal(g19,g20)
    c: Equal(g20,g18)
    c: Equal(g18,g17)
    c: Equal(g17,g16)
    c: Equal(g16,g15)
    c: PointOnObject(g4,g-1)
    c: Equal(g1,g10)
    c: Equal(g10,g14)
    c: Equal(g14,g5)
    c: Radius(g17) = 2
    c: Equal(g15,g21)
    c: Equal(g21,g22)
    c: Vertical(g11,g4)
    c: Vertical(g7,g0)
    c: Horizontal(g0,g-3)
    c: DistanceX(g0) = 24
    c: DistanceY(g1,g-1) = 24.5
    c: Horizontal(g1,g5)
    c: DistanceX(g1,g1) = 4
    c: DistanceX(g4) = 53
    c: Equal(g18,g23)
    c: PointOnObject(g8,g-4)
    c: PointOnObject(g11,g-4)
    c: PointOnObject(g6,g-1)
    c: Coincident(g27,g24)
    c: Horizontal(g25)
    c: Horizontal(g27)
    c: Vertical(g24)
    c: Vertical(g26)
    c: Horizontal(g29)
    c: Vertical(g28)
    c: Vertical(g30)
    c: Coincident(g31,g32)
    c: Coincident(g32,g33)
    c: Horizontal(g32)
    c: Horizontal(g34)
    c: Vertical(g31)
    c: Vertical(g33)
    c: Coincident(g35,g36)
    c: Coincident(g36,g37)
    c: Horizontal(g36)
    c: Horizontal(g38)
    c: Vertical(g35)
    c: Vertical(g37)
    c: Tangent(g29,g39) = 1.5708
    c: Tangent(g30,g39) = 1.5708
    c: Tangent(g28,g40) = 1.5708
    c: Tangent(g29,g40) = 1.5708
    c: Tangent(g26,g41) = 1.5708
    c: Tangent(g25,g41) = 1.5708
    c: Tangent(g24,g42) = 1.5708
    c: Tangent(g25,g42) = 1.5708
    c: Tangent(g31,g43) = 1.5708
    c: Tangent(g34,g43) = 1.5708
    c: Tangent(g33,g44) = 1.5708
    c: Tangent(g34,g44) = 1.5708
    c: Tangent(g35,g45) = 1.5708
    c: Tangent(g38,g45) = 1.5708
    c: Tangent(g37,g46) = 1.5708
    c: Tangent(g38,g46) = 1.5708
    c: Equal(g28,g35)
    c: Equal(g35,g33)
    c: Tangent(g26,g47) = 1.5708
    c: Tangent(g27,g47) = 1.5708
    c: Equal(g43,g44)
    c: Equal(g44,g42)
    c: Equal(g42,g41)
    c: Equal(g41,g40)
    c: Equal(g40,g39)
    c: Equal(g25,g34)
    c: Equal(g34,g38)
    c: Equal(g38,g29)
    c: Radius(g41) = 2
    c: Equal(g39,g45)
    c: Equal(g45,g46)
    c: Equal(g42,g47)
FEATURE [PartDesign::Pad] Pad001
  BaseFeature = -> Pocket003
  Direction = (0,0,1)
  Length = 10
  Length2 = 10
  Profile = -> Sketch008
  ReferenceAxis = -> Sketch008 [N_Axis]
  Suppressed = false
  Type = 0
